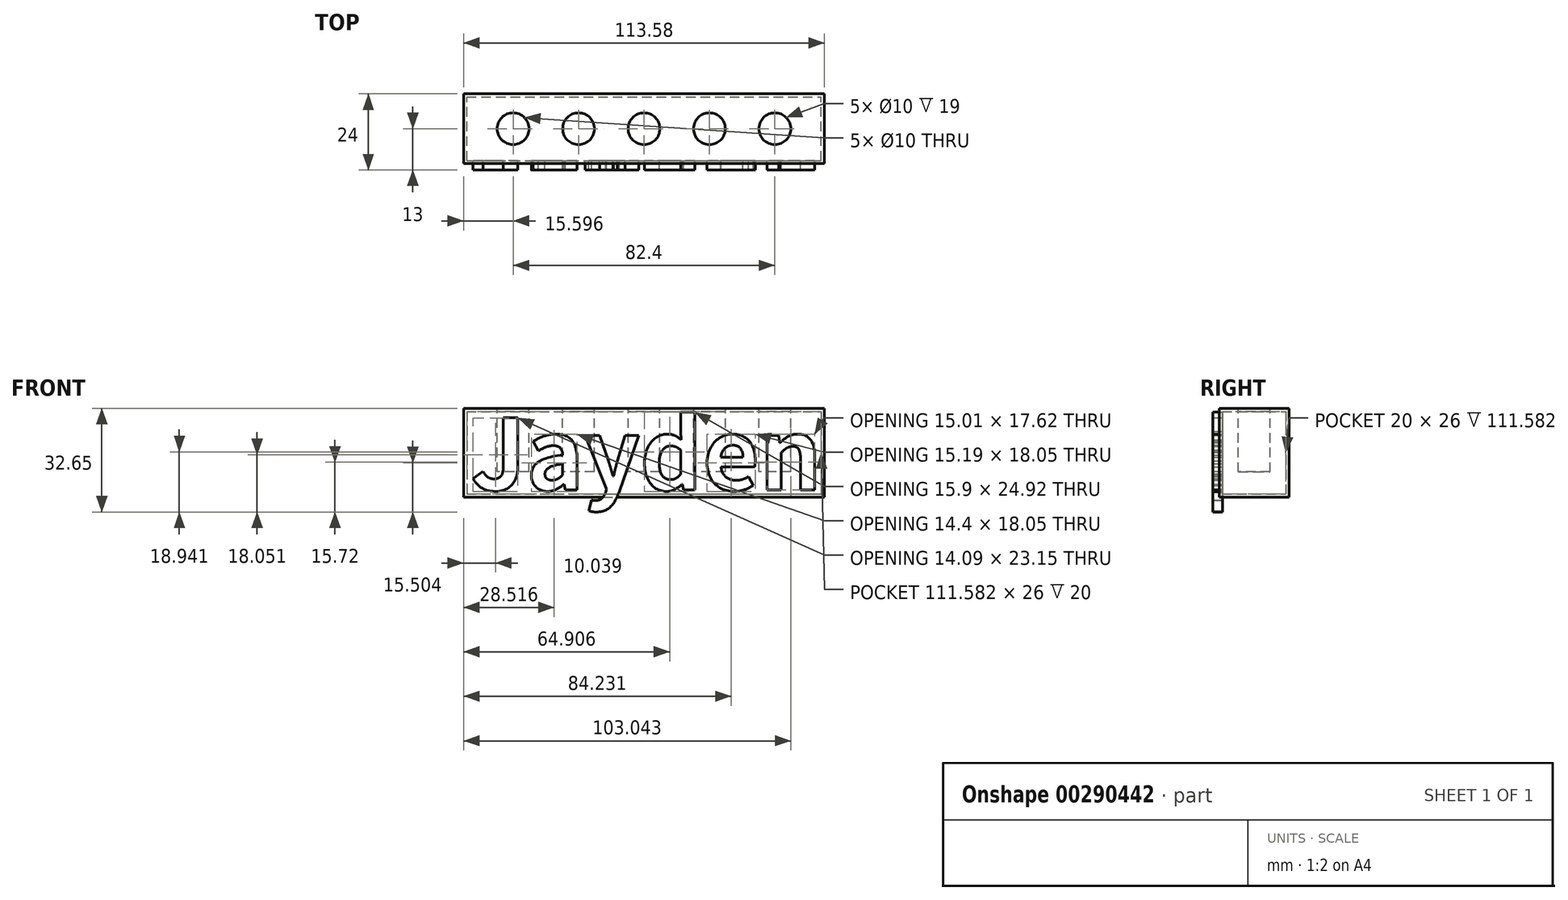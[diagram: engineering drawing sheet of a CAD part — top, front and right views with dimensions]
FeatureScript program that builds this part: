
annotation { "Feature Type Name" : "Feature", "Feature Type Description" : "" }
export const myFeature = defineFeature(function(context is Context, id is Id, definition is map)
    precondition{}
    {
        {
            var Q0;
            Q0=qCreatedBy(makeId("Front.planeOp"),FACE);
            var sketch = newSketch(context, id + "F0", { "sketchPlane" : qUnion([Q0])});
            skText(sketch, "E0", { "text": "Jayden", "fontName": "NotoSansCJKsc-Bold.otf"});
            const initialGuessF0  = {"E0": [-0.055, -0.01174, 1, 0, 0.0221]};
            skSetInitialGuess(sketch, initialGuessF0);
            skSolve(sketch);
        }
        {
            var Q0;
            Q0 = qSketchRegion(id + "F0", true);
            extrude(context, id + "F1", {"entities" : qUnion([Q0]), "depth" : 3 * mm});
        }
        {
            var Q0;
            Q0=qCreatedBy(makeId("Top.planeOp"),FACE);
            var sketch = newSketch(context, id + "F2", { "sketchPlane" : qUnion([Q0])});
            skPoint(sketch, "E1.0", {"position": v(-54.32, 0) * mm});
            skPoint(sketch, "E2.0", {"position": v(53.26, 0) * mm});
            skLineSegment(sketch, "E3.bottom", {"start": v(-56.32, 0) * mm, "end": v(55.26, 0) * mm});
            skLineSegment(sketch, "E3.top", {"start": v(-56.32, 20) * mm, "end": v(55.26, 20) * mm});
            skLineSegment(sketch, "E3.left", {"start": v(-56.32, 0) * mm, "end": v(-56.32, 20) * mm});
            skLineSegment(sketch, "E3.right", {"start": v(55.26, 0) * mm, "end": v(55.26, 20) * mm});
            skSolve(sketch);
        }
        {
            var Q0;
            Q0 = qSketchRegion(id + "F2", true);
            extrude(context, id + "F3", {"entities" : qUnion([Q0]), "operationType" : NewBodyOperationType.ADD, "endBound" : BoundingType.SYMMETRIC, "depth" : 26 * mm});
        }
        {
            var Q0;
            Q0=qCreatedBy(makeId("Top.planeOp"),FACE);
            var sketch = newSketch(context, id + "F4", { "sketchPlane" : qUnion([Q0])});
            skLineSegment(sketch, "E4.0.0", {"start": v(55.26, 20) * mm, "end": v(-56.32, 20) * mm, "construction": true});
            skLineSegment(sketch, "E4.0.1", {"start": v(-56.32, 20) * mm, "end": v(-56.32, 0) * mm, "construction": true});
            skLineSegment(sketch, "E4.0.2", {"start": v(-56.32, 0) * mm, "end": v(55.26, 0) * mm, "construction": true});
            skLineSegment(sketch, "E4.0.3", {"start": v(55.26, 0) * mm, "end": v(55.26, 20) * mm, "construction": true});
            skLineSegment(sketch, "E5.bottom", {"start": v(-57.32, 21) * mm, "end": v(56.26, 21) * mm});
            skLineSegment(sketch, "E5.top", {"start": v(-57.32, -1) * mm, "end": v(56.26, -1) * mm});
            skLineSegment(sketch, "E5.left", {"start": v(-57.32, 21) * mm, "end": v(-57.32, -1) * mm});
            skLineSegment(sketch, "E5.right", {"start": v(56.26, 21) * mm, "end": v(56.26, -1) * mm});
            skSolve(sketch);
        }
        {
            var Q0;
            Q0 = qSketchRegion(id + "F4", true);
            extrude(context, id + "F5", {"entities" : qUnion([Q0]), "endBound" : BoundingType.SYMMETRIC, "depth" : 28 * mm});
        }
        {
            var Q0;
            Q0=makeQuery(id+"F1.opExtrude","SWEPT_BODY",BODY,{"disambiguationData":[OSD([sQuery(id+"F0.wireOp",EDGE,"E0.sketch_text.stroke-0"),sQuery(id+"F0.wireOp",EDGE,"E0.sketch_text.stroke-1"),sQuery(id+"F0.wireOp",EDGE,"E0.sketch_text.stroke-2"),sQuery(id+"F0.wireOp",EDGE,"E0.sketch_text.stroke-3"),sQuery(id+"F0.wireOp",EDGE,"E0.sketch_text.stroke-4"),sQuery(id+"F0.wireOp",EDGE,"E0.sketch_text.stroke-5"),sQuery(id+"F0.wireOp",EDGE,"E0.sketch_text.stroke-6"),sQuery(id+"F0.wireOp",EDGE,"E0.sketch_text.stroke-7")])]});
            var Q1;
            Q1=makeQuery(id+"F5.opExtrude","SWEPT_BODY",BODY,{"disambiguationData":[OSD([sQuery(id+"F4.wireOp",EDGE,"E5.bottom"),sQuery(id+"F4.wireOp",EDGE,"E5.top"),sQuery(id+"F4.wireOp",EDGE,"E5.left"),sQuery(id+"F4.wireOp",EDGE,"E5.right")])]});
            booleanBodies(context, id + "F6", {"operationType" : BooleanOperationType.SUBTRACTION, "tools" : qUnion([Q0]), "targets" : qUnion([Q1]), "keepTools" : true});
        }
        {
            var Q0;
            Q0=makeQuery(id+"F5.opExtrude","CAP_FACE",FACE,{"disambiguationData":[OSD([sQuery(id+"F4.wireOp",EDGE,"E5.bottom"),sQuery(id+"F4.wireOp",EDGE,"E5.top"),sQuery(id+"F4.wireOp",EDGE,"E5.left"),sQuery(id+"F4.wireOp",EDGE,"E5.right")])],"isStart":false});
            cPlane(context, id + "F7", {"entities" : qUnion([Q0]), "cplaneType" : CPlaneType.OFFSET, "offset" : 0 * mm, "width" : 150 * mm, "height" : 150 * mm});
        }
        {
            var Q0;
            Q0=qCreatedBy(id+"F7.planeOp",FACE);
            var sketch = newSketch(context, id + "F8", { "sketchPlane" : qUnion([Q0])});
            skLineSegment(sketch, "E6.0.0", {"start": v(-57.32, 21) * mm, "end": v(-57.32, -1) * mm, "construction": true});
            skLineSegment(sketch, "E6.0.1", {"start": v(-57.32, -1) * mm, "end": v(56.26, -1) * mm, "construction": true});
            skLineSegment(sketch, "E6.0.2", {"start": v(56.26, -1) * mm, "end": v(56.26, 21) * mm, "construction": true});
            skLineSegment(sketch, "E6.0.3", {"start": v(56.26, 21) * mm, "end": v(-57.32, 21) * mm, "construction": true});
            skPoint(sketch, "E7.centerSnap0", {"position": v(-57.32, 10) * mm});
            skCircle(sketch, "E8", {"center": v(-41.72, 10) * mm, "radius": 5 * mm});
            skCircle(sketch, "E9", {"center": v(-21.12, 10) * mm, "radius": 5 * mm});
            skCircle(sketch, "E10", {"center": v(20.08, 10) * mm, "radius": 5 * mm});
            skCircle(sketch, "E11", {"center": v(40.68, 10) * mm, "radius": 5 * mm});
            skPoint(sketch, "E12", {"position": v(56.26, 10) * mm});
            skCircle(sketch, "E13", {"center": v(-0.52, 10) * mm, "radius": 5 * mm});
            skSolve(sketch);
        }
        {
            var Q0;
            Q0 = qSketchRegion(id + "F8", true);
            extrude(context, id + "F9", {"entities" : qUnion([Q0]), "operationType" : NewBodyOperationType.REMOVE, "oppositeDirection" : true, "depth" : 20 * mm});
        }
    });
